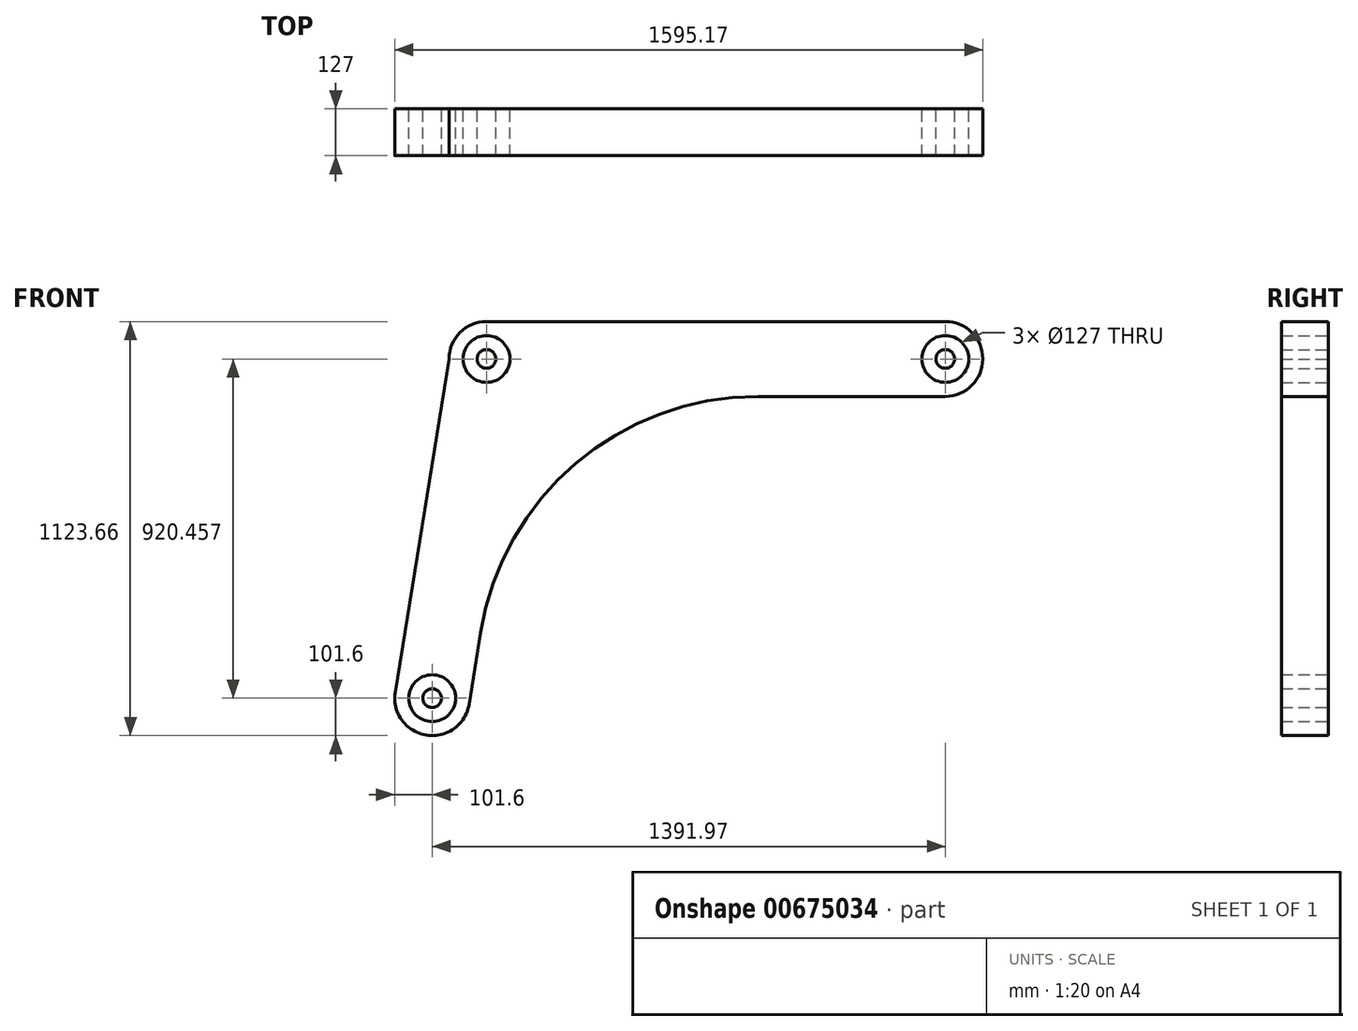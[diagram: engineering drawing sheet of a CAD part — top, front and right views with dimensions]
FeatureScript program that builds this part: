
annotation { "Feature Type Name" : "Feature", "Feature Type Description" : "" }
export const myFeature = defineFeature(function(context is Context, id is Id, definition is map)
    precondition{}
    {
        {
            var Q0;
            Q0=qCreatedBy(makeId("Front.planeOp"),FACE);
            var sketch = newSketch(context, id + "F0", { "sketchPlane" : qUnion([Q0])});
            skLineSegment(sketch, "E0", {"start": v(0, 0) * mm, "end": v(147.37, 920.46) * mm, "construction": true});
            skLineSegment(sketch, "E1", {"start": v(147.37, 920.46) * mm, "end": v(1391.97, 920.46) * mm, "construction": true});
            skLineSegment(sketch, "E2", {"start": v(1391.97, 920.46) * mm, "end": v(0, 0) * mm, "construction": true});
            skCircle(sketch, "E3", {"center": v(147.37, 920.46) * mm, "radius": 25.4 * mm});
            skCircle(sketch, "E4", {"center": v(147.37, 920.46) * mm, "radius": 63.5 * mm});
            skCircle(sketch, "E5", {"center": v(1391.97, 920.46) * mm, "radius": 63.5 * mm});
            skCircle(sketch, "E6", {"center": v(1391.97, 920.46) * mm, "radius": 25.4 * mm});
            skCircle(sketch, "E7", {"center": v(0, 0) * mm, "radius": 25.4 * mm});
            skCircle(sketch, "E8", {"center": v(0, 0) * mm, "radius": 63.5 * mm});
            skArc(sketch, "E9", {"start": v(147.37, 1022.06) * mm, "mid": v(75.53, 992.3) * mm, "end": v(45.77, 920.46) * mm});
            skArc(sketch, "E10", {"start": v(-100.3, 16.2) * mm, "mid": v(-16.13, -100.31) * mm, "end": v(100.32, -16.06) * mm});
            skArc(sketch, "E11", {"start": v(1391.97, 818.86) * mm, "mid": v(1493.57, 920.46) * mm, "end": v(1391.97, 1022.06) * mm});
            skLineSegment(sketch, "E12", {"start": v(45.77, 920.46) * mm, "end": v(-102.92, 0) * mm});
            skLineSegment(sketch, "E13", {"start": v(100.32, -16.06) * mm, "end": v(131.28, 177.32) * mm});
            skLineSegment(sketch, "E14", {"start": v(147.37, 1022.06) * mm, "end": v(1391.97, 1022.06) * mm});
            skArc(sketch, "E15", {"start": v(883.7, 818.86) * mm, "mid": v(389.3, 636.7) * mm, "end": v(131.28, 177.32) * mm});
            skLineSegment(sketch, "E16.trimOffspring", {"start": v(883.7, 818.86) * mm, "end": v(1391.97, 818.86) * mm});
            skSolve(sketch);
        }
        {
            var Q0;
            Q0=makeQuery(id+"F0.imprint","IMPRINT",FACE,{"disambiguationData":[TD([[makeQuery(id+"F0.imprint","IMPRINT",EDGE,{"derivedFrom":sQuery(id+"F0.wireOp",EDGE,"E4")}),-1.0]])]});
            var Q1;
            Q1=makeQuery(id+"F0.imprint","IMPRINT",FACE,{"disambiguationData":[TD([[makeQuery(id+"F0.imprint","IMPRINT",EDGE,{"derivedFrom":sQuery(id+"F0.wireOp",EDGE,"E3")}),1.0]])]});
            var Q2;
            Q2=makeQuery(id+"F0.imprint","IMPRINT",FACE,{"disambiguationData":[TD([[makeQuery(id+"F0.imprint","IMPRINT",EDGE,{"derivedFrom":sQuery(id+"F0.wireOp",EDGE,"E7")}),1.0]])]});
            var Q3;
            Q3=makeQuery(id+"F0.imprint","IMPRINT",FACE,{"disambiguationData":[TD([[makeQuery(id+"F0.imprint","IMPRINT",EDGE,{"derivedFrom":sQuery(id+"F0.wireOp",EDGE,"E6")}),1.0]])]});
            extrude(context, id + "F1", {"entities" : qUnion([Q0, Q1, Q2, Q3]), "depth" : 127 * mm, "offsetDistance" : 25.4 * mm});
        }
    });
